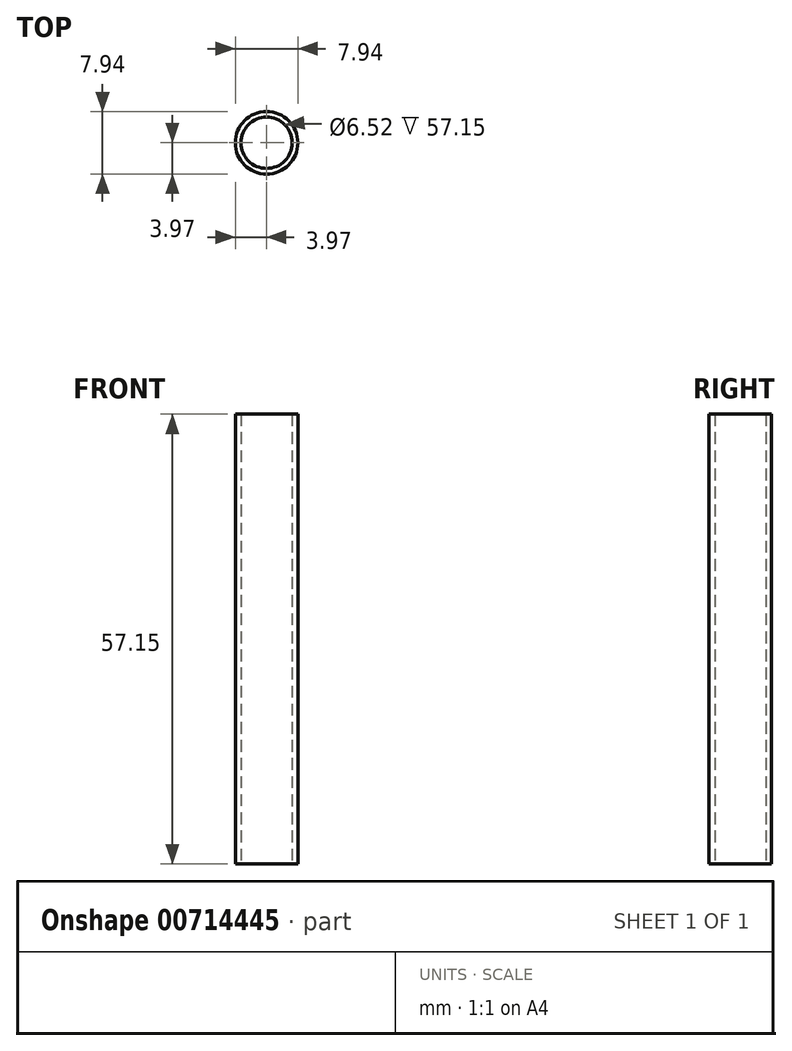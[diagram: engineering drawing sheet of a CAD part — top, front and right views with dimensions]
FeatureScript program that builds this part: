
annotation { "Feature Type Name" : "Feature", "Feature Type Description" : "" }
export const myFeature = defineFeature(function(context is Context, id is Id, definition is map)
    precondition{}
    {
        {
            var Q0;
            Q0=qCreatedBy(makeId("Top.planeOp"),FACE);
            var sketch = newSketch(context, id + "F0", { "sketchPlane" : qUnion([Q0])});
            skCircle(sketch, "E0", {"center": v(0, 0) * mm, "radius": 3.26 * mm});
            skCircle(sketch, "E1", {"center": v(0, 0) * mm, "radius": 3.97 * mm});
            skSolve(sketch);
        }
        {
            var Q0;
            Q0=makeQuery(id+"F0.imprint","IMPRINT",FACE,{"disambiguationData":[TD([[makeQuery(id+"F0.imprint","IMPRINT",EDGE,{"derivedFrom":sQuery(id+"F0.wireOp",EDGE,"E0")}),-1.0]])]});
            extrude(context, id + "F1", {"entities" : qUnion([Q0]), "depth" : 57.15 * mm});
        }
    });
